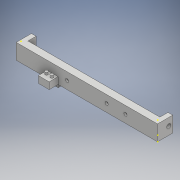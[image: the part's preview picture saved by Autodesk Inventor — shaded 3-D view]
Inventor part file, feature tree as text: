
AUTODESK INVENTOR PART (.ipt)
format: ipt  version: 2018 (Build 220112000, 112)  size: 288,256 bytes
history: native  units: mm
features: sketch x22, extrude x18, fillet x4
ambient origin geometry x8: Origin, YZ Plane, XZ Plane, XY Plane, X Axis, Y Axis, Z Axis, Center Point
bodies: Solid1 (feature_tree)
feature tree (44):
  extrude  "Extrusion1"  Depth=19.925mm
  extrude  "Extrusion2"  Depth=5.0mm
  extrude  "Extrusion3"  Depth=12.175mm TaperAngle=0.0deg
  extrude  "Extrusion4"  Depth=4.65mm TaperAngle=0.0deg
  sketch  "Sketch5"  dims[d11=10.5mm d12=2.75mm]
  extrude  "Extrusion5"  Depth=2.75mm
  extrude  "Extrusion6"  Depth=3.5mm
  extrude  "Extrusion7"  Depth=4.5mm
  fillet  "Fillet1"  Radius=5.0mm
  fillet  "Fillet2"  Radius=3.8mm
  extrude  "Extrusion8"  Depth=3.0mm
  extrude  "Extrusion9"  Depth=3.3mm
  fillet  "Fillet3"  Radius=21.0mm
  extrude  "Extrusion10"  Depth=4.0mm TaperAngle=0.0deg
  sketch  "Sketch12"  dims[d36=3.3mm d37=4.0mm d38=0.0mm]
  sketch  "Sketch13"  dims[d39=3.3mm d40=4.0mm d41=0.0mm]
  extrude  "Extrusion11"  Depth=4.0mm TaperAngle=0.0deg
  extrude  "Extrusion12"  Depth=9.5mm
  extrude  "Extrusion13"  Depth=11.5mm
  sketch  "Sketch16"  dims[d46=9.5mm d47=0.0mm d48=4.0mm]
  sketch  "Sketch17"  dims[d49=6.175mm d50=0.0mm d51=1.825mm d52=0.0mm]
  extrude  "Extrusion14"  Depth=4.0mm
  extrude  "Extrusion15"  Depth=1.825mm TaperAngle=0.0deg
  extrude  "Extrusion16"  Depth=4.5mm TaperAngle=0.0deg
  extrude  "Extrusion17"  Depth=9.5mm TaperAngle=0.0deg
  extrude  "Extrusion18"  Depth=7.5mm
  fillet  "Fillet4"  Radius=2.88mm
  sketch  "Sketch1"  dims[d0=150.0mm d1=19.925mm]
  sketch  "Sketch2"  dims[d2=4.0mm d3=0.0mm d4=5.0mm]
  sketch  "Sketch3"  dims[d5=5.0mm d6=12.175mm d7=0.0mm]
  sketch  "Sketch4"  dims[d8=3.2mm d9=4.65mm d10=0.0mm]
  sketch  "Sketch6"  dims[d13=3.5mm d14=0.0mm d15=7.95mm]
  sketch  "Sketch7"  dims[d16=7.95mm d17=4.5mm]
  sketch  "Sketch8"  dims[d18=155.75mm d19=5.75mm d20=0.0mm d21=0.0mm]
  sketch  "Sketch9"  dims[d22=21.0mm d23=34.875mm d24=0.0mm d25=0.0mm d26=5.0mm d27=3.8mm d28=0.0mm]
  sketch  "Sketch10"  dims[d29=3.0mm d30=3.0mm]
  sketch  "Sketch11"  dims[d33=21.0mm d34=3.3mm d35=21.0mm]
  sketch  "Sketch14"  dims[d42=2.0mm d43=9.5mm]
  sketch  "Sketch15"  dims[d44=5.0mm d45=11.5mm]
  sketch  "Sketch18"  dims[d53=0.5mm d54=0.0mm d55=4.5mm d56=0.0mm]
  sketch  "Sketch19"  dims[d57=4.0mm d58=9.5mm d59=0.0mm]
  sketch  "Sketch20"  dims[d60=7.5mm d61=2.88mm d62=2.88mm]
  sketch  "Sketch21"  dims[d63=3.0mm]
  sketch  "Sketch22"  dims[d64=3.0mm d65=2.5mm d66=0.0mm d67=2.5mm d68=3.0mm d69=0.0mm d70=2.0mm d71=2.5mm d72=0.0mm d73=1.0mm]
